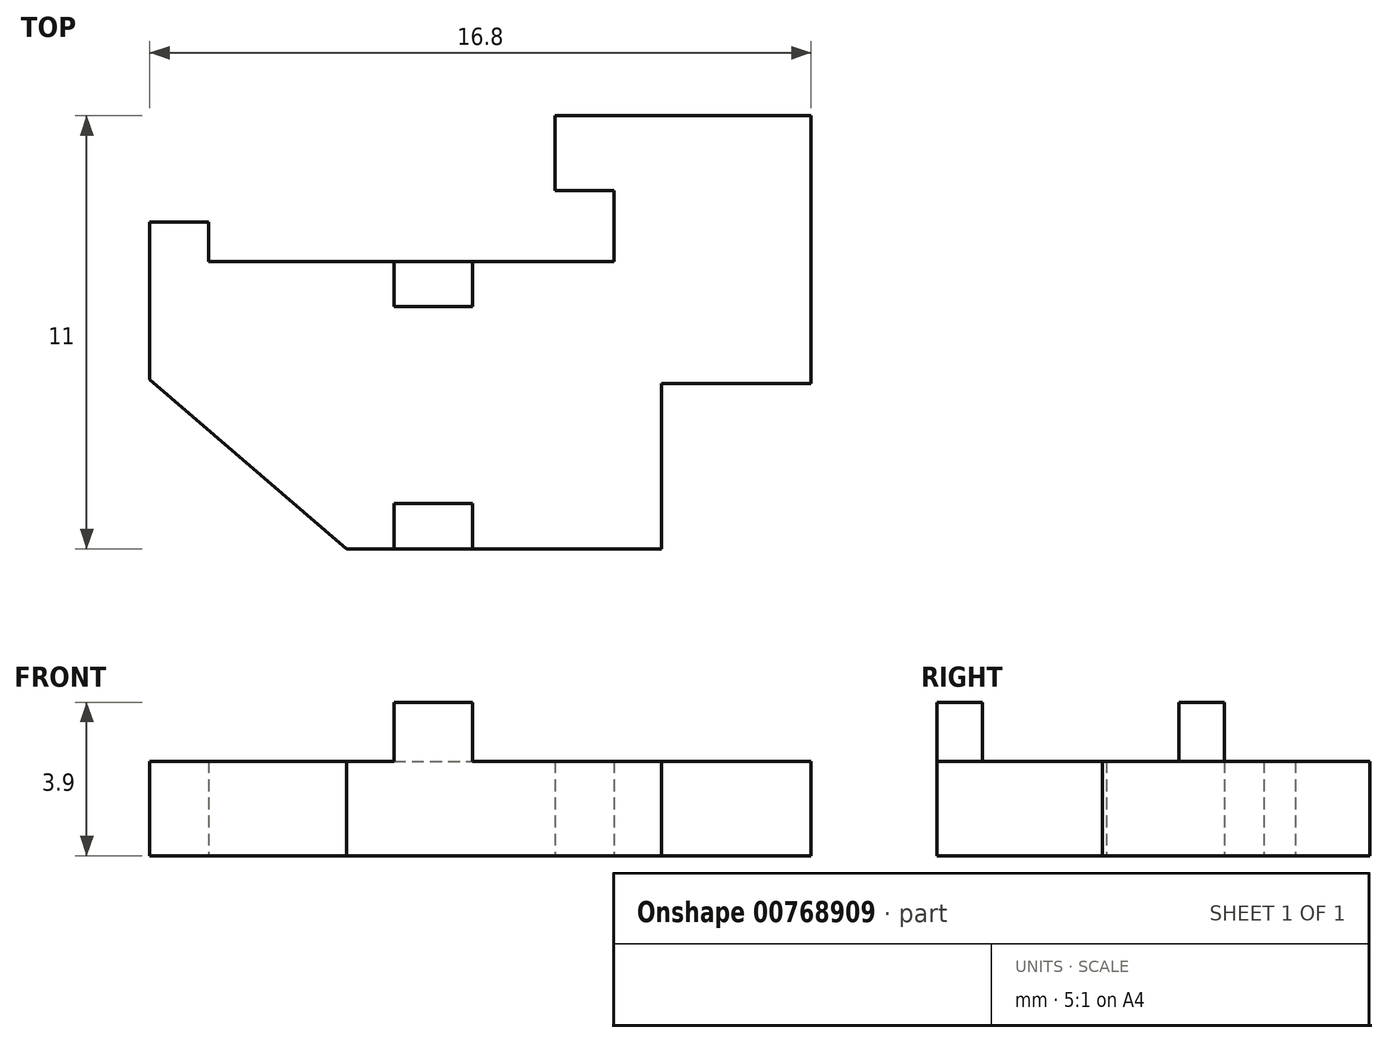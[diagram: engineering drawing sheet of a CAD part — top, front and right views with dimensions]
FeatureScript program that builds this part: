
annotation { "Feature Type Name" : "Feature", "Feature Type Description" : "" }
export const myFeature = defineFeature(function(context is Context, id is Id, definition is map)
    precondition{}
    {
        {
            var Q0;
            Q0=qCreatedBy(makeId("Top.planeOp"),FACE);
            var sketch = newSketch(context, id + "F0", { "sketchPlane" : qUnion([Q0])});
            skLineSegment(sketch, "E0", {"start": v(0, 0) * mm, "end": v(0, 4.2) * mm, "construction": true});
            skLineSegment(sketch, "E1", {"start": v(0, 11) * mm, "end": v(-6.5, 11) * mm});
            skLineSegment(sketch, "E2", {"start": v(-6.5, 11) * mm, "end": v(-6.5, 9.1) * mm});
            skLineSegment(sketch, "E3", {"start": v(-6.5, 9.1) * mm, "end": v(-5, 9.1) * mm});
            skLineSegment(sketch, "E4", {"start": v(-5, 9.1) * mm, "end": v(-5, 7.3) * mm});
            skLineSegment(sketch, "E5", {"start": v(-5, 7.3) * mm, "end": v(-15.3, 7.3) * mm});
            skLineSegment(sketch, "E6", {"start": v(-15.3, 7.3) * mm, "end": v(-15.3, 8.3) * mm});
            skLineSegment(sketch, "E7", {"start": v(-15.3, 8.3) * mm, "end": v(-16.8, 8.3) * mm});
            skLineSegment(sketch, "E8", {"start": v(-16.8, 8.3) * mm, "end": v(-16.8, 4.3) * mm});
            skLineSegment(sketch, "E9", {"start": v(-16.8, 4.3) * mm, "end": v(-11.8, 0) * mm});
            skLineSegment(sketch, "E10", {"start": v(-3.8, 0) * mm, "end": v(-3.8, 0) * mm});
            skLineSegment(sketch, "E11", {"start": v(-3.8, 4.2) * mm, "end": v(0, 4.2) * mm});
            skLineSegment(sketch, "E12", {"start": v(0, 4.2) * mm, "end": v(0, 11) * mm});
            skLineSegment(sketch, "E13", {"start": v(-3.8, 0) * mm, "end": v(-3.8, 4.2) * mm});
            skLineSegment(sketch, "E14", {"start": v(-11.8, 0) * mm, "end": v(-3.8, 0) * mm});
            skLineSegment(sketch, "E15", {"start": v(-3.8, 0) * mm, "end": v(0, 0) * mm, "construction": true});
            skSolve(sketch);
        }
        {
            var Q0;
            Q0=qSketchRegion(id+"F0",true);
            extrude(context, id + "F1", {"entities" : qUnion([Q0]), "endBound" : BoundingType.SYMMETRIC, "depth" : 2.4 * mm, "offsetDistance" : 25 * mm});
        }
        {
            var Q0;
            Q0=makeQuery(id+"F1.opExtrude","CAP_FACE",FACE,{"disambiguationData":[OSD([sQuery(id+"F0.wireOp",EDGE,"E0"),sQuery(id+"F0.wireOp",EDGE,"E1"),sQuery(id+"F0.wireOp",EDGE,"E2"),sQuery(id+"F0.wireOp",EDGE,"E3"),sQuery(id+"F0.wireOp",EDGE,"E4"),sQuery(id+"F0.wireOp",EDGE,"E5"),sQuery(id+"F0.wireOp",EDGE,"E6"),sQuery(id+"F0.wireOp",EDGE,"E7"),sQuery(id+"F0.wireOp",EDGE,"E8"),sQuery(id+"F0.wireOp",EDGE,"E9"),sQuery(id+"F0.wireOp",EDGE,"6ygt5FA0-rvqF-1QtY-5Llw-hZYWhaoFuQCv")])],"isStart":false});
            var sketch = newSketch(context, id + "F2", { "sketchPlane" : qUnion([Q0])});
            skLineSegment(sketch, "E16.bottom", {"start": v(-8.6, 0) * mm, "end": v(-10.6, 0) * mm});
            skLineSegment(sketch, "E16.top", {"start": v(-8.6, 1.15) * mm, "end": v(-10.6, 1.15) * mm});
            skLineSegment(sketch, "E16.left", {"start": v(-8.6, 0) * mm, "end": v(-8.6, 1.15) * mm});
            skLineSegment(sketch, "E16.right", {"start": v(-10.6, 0) * mm, "end": v(-10.6, 1.15) * mm});
            skLineSegment(sketch, "E17.bottom", {"start": v(-10.6, 7.3) * mm, "end": v(-8.6, 7.3) * mm});
            skLineSegment(sketch, "E17.top", {"start": v(-10.6, 6.15) * mm, "end": v(-8.6, 6.15) * mm});
            skLineSegment(sketch, "E17.left", {"start": v(-10.6, 7.3) * mm, "end": v(-10.6, 6.15) * mm});
            skLineSegment(sketch, "E17.right", {"start": v(-8.6, 7.3) * mm, "end": v(-8.6, 6.15) * mm});
            skLineSegment(sketch, "E18", {"start": v(-8.6, 1.15) * mm, "end": v(-8.6, 6.15) * mm, "construction": true});
            skSolve(sketch);
        }
        {
            var Q0;
            Q0=qSketchRegion(id+"F2",true);
            extrude(context, id + "F3", {"entities" : qUnion([Q0]), "operationType" : NewBodyOperationType.ADD, "depth" : 1.5 * mm, "offsetDistance" : 25 * mm});
        }
    });
